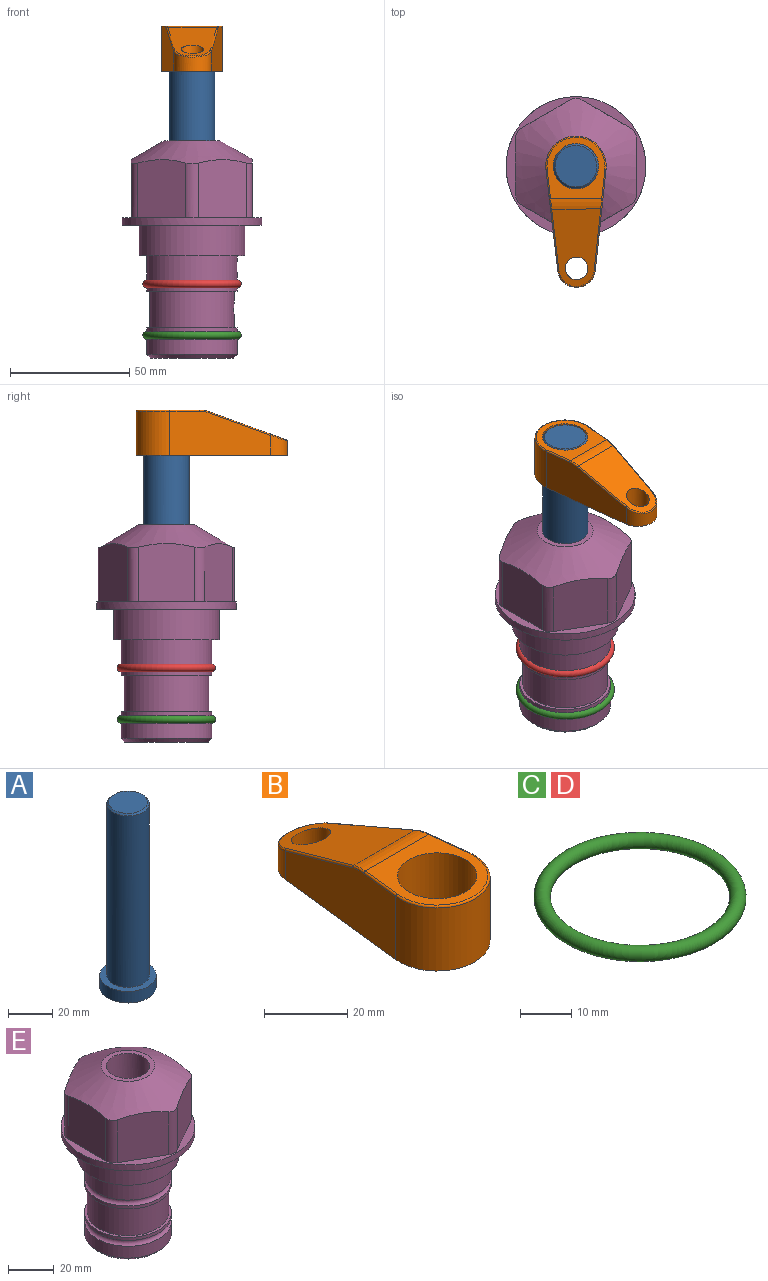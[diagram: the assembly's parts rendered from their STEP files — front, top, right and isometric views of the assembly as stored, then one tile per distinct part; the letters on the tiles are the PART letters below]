
ASSEMBLY  parts=5 mates=3
PART A: 6 faces, bbox 25.4x25.4x101.6 mm
  f0: plane 17.46x17.46mm, normal (0,0,1), area 239.5mm2, adj f5
  f1: plane 25.4x25.4mm, normal (0,0,-1), area 506.7mm2, adj f2
  f2: cylinder r=12.7mm len=25.4mm, axis (0,0,1), area 506.7mm2, adj f1,f3
  f3: plane 25.4x25.4mm, normal (0,0,1), area 221.7mm2, adj f2,f4
  f4: cylinder r=9.53mm len=94.46mm, axis (0,0,1), area 5653mm2, adj f3,f5
  f5: cone r=8.73mm half-angle=45deg, axis (0,0,-1), area 64.4mm2, adj f0,f4
PART B: 44 faces, bbox 27.5x64.5x19.1 mm
  f0: plane 2.3x0.95mm, normal (0,0,-1), area 1mm2, adj f25,f30,f34
  f1: plane 63.5x25.4mm, normal (0,0,-1), area 561.7mm2, adj f2,f3,f4,f5,f6,f7,f19,f20
  f2: cylinder r=12.7mm len=25.4mm, axis (0,0,-1), area 792.2mm2, adj f1,f3,f5,f13
  f3: plane 42.33x18.54mm, normal (0.99,0.11,0), area 647mm2, adj f1,f2,f4,f11,f12,f14
  f4: cylinder r=7.94mm len=15.78mm, axis (0,0,-1), area 158.6mm2, adj f1,f3,f5,f16
  f5: plane 42.33x18.54mm, normal (-0.99,0.11,0), area 647mm2, adj f1,f2,f4,f15,f17,f18
  f6: cylinder r=9.53mm len=19.05mm, axis (0,0,-1), area 1140.1mm2, adj f1,f8
  f7: cylinder r=4.76mm len=10.98mm, axis (0,0,-1), area 276.1mm2, adj f1,f9
  f8: plane 25.83x24.38mm, normal (0,0,1), area 262.2mm2, adj f6,f10,f11,f13,f15
  f9: plane 32.49x20.55mm, normal (0,0.34,0.94), area 489.9mm2, adj f7,f10,f14,f16,f18
  f10: cylinder r=12.7mm len=21.49mm, axis (-1,0,0), area 93.2mm2, adj f8,f9,f12,f17
  f11: cylinder r=0.51mm len=12.34mm, axis (0.11,-0.99,0), area 9.9mm2, adj f3,f8,f12,f13
  f12: bspline ~7.62x1.64mm, area 3.5mm2, adj f3,f10,f11,f14
  f13: torus R=12.19mm, axis (0,0,1), area 33.6mm2, adj f2,f8,f11,f15
  f14: cylinder r=0.51mm len=26.01mm, axis (0.1,-0.93,0.34), area 21.6mm2, adj f3,f9,f12,f16
  f15: cylinder r=0.51mm len=12.34mm, axis (0.11,0.99,0), area 9.9mm2, adj f5,f8,f13,f17
  f16: bspline ~15.78x7.05mm, area 15.7mm2, adj f4,f9,f14,f18
  f17: bspline ~7.62x1.64mm, area 3.5mm2, adj f5,f10,f15,f18
  f18: cylinder r=0.51mm len=26.01mm, axis (0.1,0.93,-0.34), area 21.6mm2, adj f5,f9,f16,f17
  f19: plane 21.6x14.29mm, normal (-0.99,-0.11,0), area 242.6mm2, adj f1,f26,f28,f34,f36,f38
  f20: plane 21.6x14.29mm, normal (0.99,-0.11,0), area 242.6mm2, adj f1,f27,f29,f37,f39,f41
  f21: cylinder r=12.7mm len=14.29mm, axis (0,0,-1), area 173.2mm2, adj f1,f26,f27,f30,f31,f33
  f22: cylinder r=7.94mm len=7.63mm, axis (0,0,-1), area 53.8mm2, adj f1,f28,f29,f42
  f23: plane 2.3x0.95mm, normal (0,0,-1), area 1mm2, adj f25,f33,f37
  f24: plane 17.94x12.32mm, normal (0,-0.34,-0.94), area 191.2mm2, adj f25,f38,f41,f42
  f25: cylinder r=9.53mm len=12.93mm, axis (-1,0,0), area 37.5mm2, adj f0,f23,f24,f31,f36,f39
  f26: cylinder r=1.59mm len=14.29mm, axis (0,0,-1), area 49mm2, adj f1,f19,f21,f32
  f27: cylinder r=1.59mm len=14.29mm, axis (0,0,-1), area 49mm2, adj f1,f20,f21,f35
  f28: cylinder r=1.59mm len=7.28mm, axis (0,0,-1), area 22.1mm2, adj f1,f19,f22,f40
  f29: cylinder r=1.59mm len=7.28mm, axis (0,0,-1), area 22.1mm2, adj f1,f20,f22,f43
  f30: torus R=14.29mm, axis (0,0,1), area 5.8mm2, adj f0,f21,f31,f32
  f31: bspline ~11.06x2.73mm, area 20.8mm2, adj f21,f25,f30,f33
  f32: sphere r=1.59mm, area 5.4mm2, adj f26,f30,f34
  f33: torus R=14.29mm, axis (0,0,1), area 5.8mm2, adj f21,f23,f31,f35
  f34: cylinder r=1.59mm len=1.68mm, axis (-0.11,0.99,0), area 2.4mm2, adj f0,f19,f32,f36
  f35: sphere r=1.59mm, area 5.4mm2, adj f27,f33,f37
  f36: bspline ~5.82x2.33mm, area 7.7mm2, adj f19,f25,f34,f38
  f37: cylinder r=1.59mm len=1.68mm, axis (0.11,0.99,0), area 2.4mm2, adj f20,f23,f35,f39
  f38: cylinder r=1.59mm len=18.33mm, axis (0.1,-0.93,0.34), area 46.7mm2, adj f19,f24,f36,f40
  f39: bspline ~5.82x2.33mm, area 7.7mm2, adj f20,f25,f37,f41
  f40: sphere r=1.59mm, area 3.6mm2, adj f28,f38,f42
  f41: cylinder r=1.59mm len=18.33mm, axis (0.1,0.93,-0.34), area 46.7mm2, adj f20,f24,f39,f43
  f42: bspline ~8.31x1.84mm, area 15.3mm2, adj f22,f24,f40,f43
  f43: sphere r=1.59mm, area 3.6mm2, adj f29,f41,f42
PART C: 1 faces, bbox 44.7x44.7x3.2 mm
  f0: torus R=19.05mm, axis (0,0,1), area 1193.9mm2
PART D: same geometry as C
PART E: 36 faces, bbox 58.7x58.7x91.2 mm
  f0: cylinder r=17.78mm len=35.56mm, axis (0,0,1), area 1670.8mm2, adj f23,f24,f31
  f1: cylinder r=19.05mm len=38.1mm, axis (0,0,1), area 1191.9mm2, adj f26,f27,f30
  f2: plane 58.66x58.66mm, normal (0,0,-1), area 1150.6mm2, adj f3,f28
  f3: cylinder r=29.33mm len=58.66mm, axis (0,0,-1), area 585.1mm2, adj f2,f4
  f4: plane 58.66x58.66mm, normal (0,0,1), area 475.9mm2, adj f3,f5,f6,f7,f8,f9,f10,f11
  f5: plane 24.5x20.32mm, normal (-0.5,0.87,0), area 562.8mm2, adj f4,f15,f16,f17
  f6: plane 24.5x20.32mm, normal (0.5,0.87,0), area 562.8mm2, adj f4,f14,f15,f17
  f7: plane 24.5x23.48mm, normal (1,0,0), area 562.8mm2, adj f4,f13,f14,f17
  f8: plane 24.5x20.32mm, normal (0.5,-0.87,0), area 562.8mm2, adj f4,f12,f13,f17
  f9: plane 24.5x20.32mm, normal (-0.5,-0.87,0), area 562.8mm2, adj f4,f11,f12,f17
  f10: plane 24.5x23.48mm, normal (-1,0,0), area 562.8mm2, adj f4,f11,f16,f17
  f11: cylinder r=5.08mm len=23.01mm, axis (0,0,-1), area 121.2mm2, adj f4,f9,f10,f17
  f12: cylinder r=5.08mm len=23.01mm, axis (0,0,-1), area 121.2mm2, adj f4,f8,f9,f17
  f13: cylinder r=5.08mm len=23.01mm, axis (0,0,-1), area 121.2mm2, adj f4,f7,f8,f17
  f14: cylinder r=5.08mm len=23.01mm, axis (0,0,-1), area 121.2mm2, adj f4,f6,f7,f17
  f15: cylinder r=5.08mm len=23.01mm, axis (0,0,-1), area 121.2mm2, adj f4,f5,f6,f17
  f16: cylinder r=5.08mm len=23.01mm, axis (0,0,-1), area 121.2mm2, adj f4,f5,f10,f17
  f17: cone r=11.73mm half-angle=60deg, axis (0,0,-1), area 2071.8mm2, adj f5,f6,f7,f8,f9,f10,f11,f12
  f18: plane 23.46x23.46mm, normal (0,0,1), area 147.4mm2, adj f17,f35
  f19: plane 34.93x34.93mm, normal (0,0,-1), area 958mm2, adj f29
  f20: cylinder r=19.05mm len=38.1mm, axis (0,0,1), area 760.1mm2, adj f21,f29
  f21: torus R=19.05mm, axis (0,0,1), area 565.3mm2, adj f20,f22
  f22: cylinder r=19.05mm len=38.1mm, axis (0,0,1), area 190mm2, adj f21,f23
  f23: plane 38.1x38.1mm, normal (0,0,1), area 146.9mm2, adj f0,f22
  f24: plane 38.1x38.1mm, normal (0,0,-1), area 146.9mm2, adj f0,f25
  f25: cylinder r=19.05mm len=38.1mm, axis (0,0,1), area 190mm2, adj f24,f26
  f26: torus R=19.05mm, axis (0,0,1), area 565.3mm2, adj f1,f25
  f27: plane 44.45x44.45mm, normal (0,0,-1), area 411.7mm2, adj f1,f28
  f28: cylinder r=22.23mm len=44.45mm, axis (0,0,1), area 1773.5mm2, adj f2,f27
  f29: cone r=19.05mm half-angle=45deg, axis (0,0,1), area 257.5mm2, adj f19,f20
  f30: cylinder r=3.17mm len=6.75mm, axis (-1,0,0), area 128mm2, adj f1,f33
  f31: cylinder r=3.17mm len=6.35mm, axis (-1,0,0), area 102.5mm2, adj f0,f33
  f32: plane 25.4x25.4mm, normal (0,0,1), area 506.7mm2, adj f33
  f33: cylinder r=12.7mm len=66.42mm, axis (0,0,-1), area 5236.2mm2, adj f30,f31,f32,f34
  f34: cone r=9.53mm half-angle=30deg, axis (0,0,-1), area 443.4mm2, adj f33,f35
  f35: cylinder r=9.53mm len=19.05mm, axis (0,0,-1), area 849mm2, adj f18,f34
PLACE A rot(axis=(0,0,-1),89.7deg) t=(0,0,10.08)mm
PLACE B rot(axis=(0,0,-1),179.7deg) t=(0,0,64.69)mm
PLACE C t=(0,0,-21.59)mm
PLACE D at identity
PLACE E at identity fixed
MATE fastened C.f0 <-> E.f0  axis (0,0,1) through (0,0,-46.1)mm
MATE cylindrical A.f2 <-> E.f0  axis (0,0,1) through (0,0,35.72)mm
MATE fastened B.f2 <-> A.f2  axis (0,0,1) through (0,0,83.74)mm
